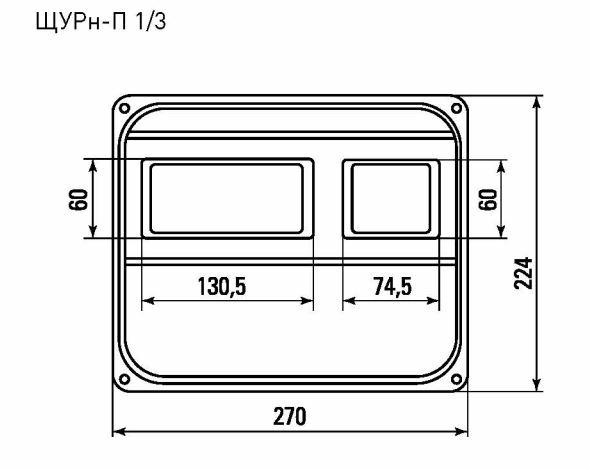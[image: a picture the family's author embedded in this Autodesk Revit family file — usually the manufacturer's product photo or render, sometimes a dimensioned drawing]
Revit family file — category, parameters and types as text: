
# Revit family: EKF_EE_ЭкранКожухаРубильникаВРУUNIT_PROxima
name_source: partatom
category: Электрооборудование
units: mm (PartAtom-declared; Revit-internal decimal feet)

## family parameters
Всегда вертикально = Нет
На основе рабочей плоскости = Да
Общий = Да
При загрузке вырезать с полостями = Нет
Размер круглого соединителя = Использовать диаметр
Тип детали = Силовой щит
Точка расчета площади = Нет

## types (3) — shared parameters
ADSK_Единица измерения = шт.
ADSK_Завод-изготовитель = EKF
ADSK_Количество = 1
ADSK_Марка = Экран для кожуха рубильника
ADSK_Материал = Акрил, прозрачный красный
ADSK_Обозначение = Экран для кожуха рубильника
ADSK_Размер_Высота = 250 мм
ADSK_Размер_Глубина = 2 мм
h = 250 мм
t = 2 мм
Изготовитель = EKF
Отметка по умолчанию = 1219.2 мм
Отступ1 = 30 мм
ОтступОтв = 11.5 мм
Серия номенклатуры = Unit PROxima
Степень защиты IP = -
ТВ = EKF_2
Тип установки = -
zero-valued in all types: ADSK_Масса

## per-type parameters (varying)
| type | ADSK_Код изделия | ADSK_Размер_Ширина | Тип | Ширина |
| Экран для кожуха рубильника для ВРУ Unit шириной 450мм EKF PROxima | mb-15-kr-45 | 180 мм | 82 мм | 180 мм |
| Экран для кожуха рубильника для ВРУ Unit шириной 600мм EKF PROxima | mb-15-kr-60 | 330 мм | 83 мм | 330 мм |
| Экран для кожуха рубильника для ВРУ Unit шириной 800мм EKF PROxima | mb-15-kr-80 | 530 мм | 84 мм | 530 мм |

note: column(s) folded — value = type name in every type: ADSK_Наименование
